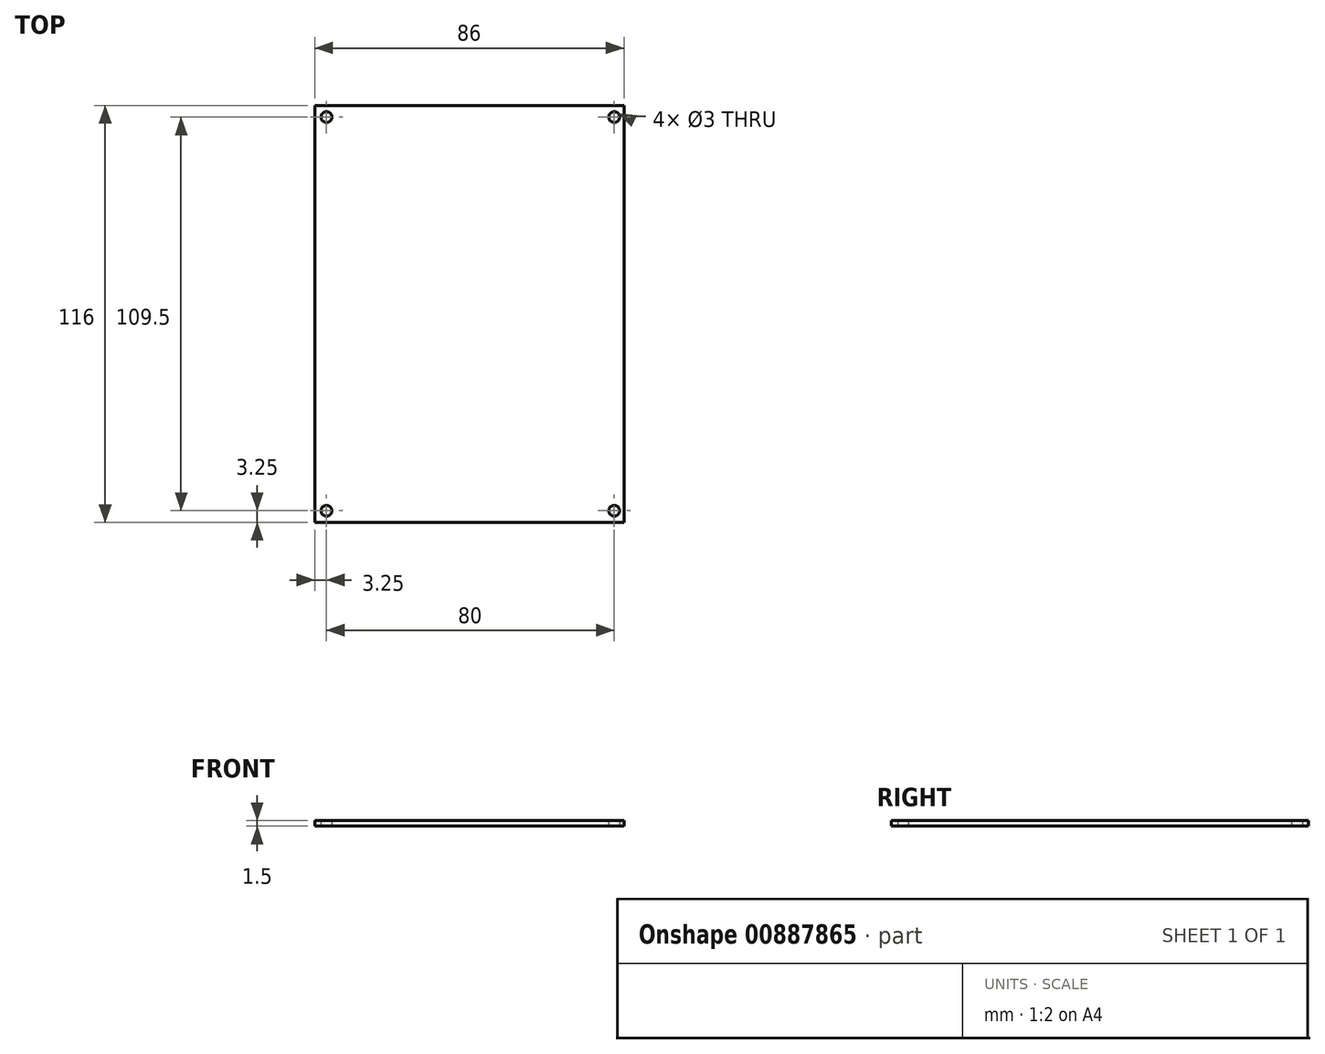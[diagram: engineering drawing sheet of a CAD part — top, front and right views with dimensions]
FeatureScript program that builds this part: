
annotation { "Feature Type Name" : "Feature", "Feature Type Description" : "" }
export const myFeature = defineFeature(function(context is Context, id is Id, definition is map)
    precondition{}
    {
        {
            var Q0;
            Q0=qCreatedBy(makeId("Top.planeOp"),FACE);
            var sketch = newSketch(context, id + "F0", { "sketchPlane" : qUnion([Q0])});
            skLineSegment(sketch, "E0.bottom", {"start": v(43, -58) * mm, "end": v(-43, -58) * mm});
            skLineSegment(sketch, "E0.top", {"start": v(43, 58) * mm, "end": v(-43, 58) * mm});
            skLineSegment(sketch, "E0.left", {"start": v(43, -58) * mm, "end": v(43, 58) * mm});
            skLineSegment(sketch, "E0.right", {"start": v(-43, -58) * mm, "end": v(-43, 58) * mm});
            skPoint(sketch, "E1.middle", {"position": v(0, 0) * mm});
            skCircle(sketch, "E2", {"center": v(40.25, 54.75) * mm, "radius": 1.5 * mm});
            skCircle(sketch, "E3", {"center": v(40.25, -54.75) * mm, "radius": 1.5 * mm});
            skCircle(sketch, "E4", {"center": v(-39.75, -54.75) * mm, "radius": 1.5 * mm});
            skCircle(sketch, "E5", {"center": v(-39.75, 54.75) * mm, "radius": 1.5 * mm});
            skLineSegment(sketch, "E6.bottom", {"start": v(40.25, -54.75) * mm, "end": v(-39.75, -54.75) * mm, "construction": true});
            skLineSegment(sketch, "E6.top", {"start": v(40.25, 54.75) * mm, "end": v(-39.75, 54.75) * mm, "construction": true});
            skLineSegment(sketch, "E6.left", {"start": v(40.25, -54.75) * mm, "end": v(40.25, 54.75) * mm, "construction": true});
            skLineSegment(sketch, "E6.right", {"start": v(-39.75, -54.75) * mm, "end": v(-39.75, 54.75) * mm, "construction": true});
            skPoint(sketch, "E6.middle", {"position": v(0.25, 0) * mm});
            skLineSegment(sketch, "E7", {"start": v(-39.75, 54.75) * mm, "end": v(-39.75, 58) * mm, "construction": true});
            skLineSegment(sketch, "E8", {"start": v(-39.75, 54.75) * mm, "end": v(-43, 54.75) * mm, "construction": true});
            skSolve(sketch);
        }
        {
            var Q0;
            Q0=qSketchRegion(id+"F0",true);
            extrude(context, id + "F1", {"entities" : qUnion([Q0]), "depth" : 1.5 * mm, "offsetDistance" : 25 * mm});
        }
    });
